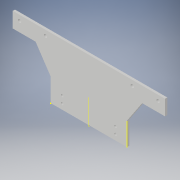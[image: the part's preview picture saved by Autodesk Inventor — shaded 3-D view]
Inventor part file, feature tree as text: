
AUTODESK INVENTOR PART (.ipt)
format: ipt  version: 2017 (Build 210142000, 142)  size: 143,872 bytes
history: native  units: in
note: dims shown in document units (in); Inventor stores cm internally (conversion verified against a paired STEP export)
features: sketch x13, hole x2, extrude x1, plane x1, mirror x1
ambient origin geometry x8: Origin, YZ Plane, XZ Plane, XY Plane, X Axis, Y Axis, Z Axis, Center Point
bodies: Solid1 (feature_tree)
feature tree (18):
  sketch  "Sketch1"  dims[d0=3.937in d1=7.874in]
  sketch  "Sketch2"  dims[d2=0.0in d3=0.7874in]
  sketch  "Sketch3"  dims[d4=1.1811in d5=1.1811in]
  sketch  "Sketch4"  dims[d6=0.7874in]
  extrude  "Extrusion1"  Depth=7.874in
  sketch  "Sketch6"  dims[d7=1.1811in]
  sketch  "Sketch7"  dims[d8=1.1811in]
  sketch  "Sketch8"  dims[d9=0.7874in]
  hole  "Hole2"  [1 undecoded]
  sketch  "Sketch11"  dims[d11=0.1181in d12=0.0in]
  hole  "Hole3"  [1 undecoded]
  plane  "Work Plane2"
  mirror  "Mirror1"
  sketch  "Sketch14"  dims[d38=0.5906in]
  sketch  "Sketch15"  dims[d39=0.2756in]
  sketch  "Sketch16"  dims[d40=0.3543in d42=0.1339in d43=0.2362in d44=0.1575in d45=0.0787in d46=90.0deg d47=0.315in d48=0.8108in d50=0.3543in d51=1.3386in d52=0.2756in d53=0.2756in d54=0.1732in d55=0.2362in d56=0.1575in d57=0.0787in d58=90.0deg d59=0.315in d60=0.8108in d62=-1.9685in]
  sketch  "Sketch9"  dims[d10=0.7874in]
  sketch  "Sketch12"  dims[d37=0.5906in]
note: 2 required parameter values undecoded (feature->parameter linkage not recoverable at this tier; creation-order binding heuristic only, values carry confidence <= 0.55)
